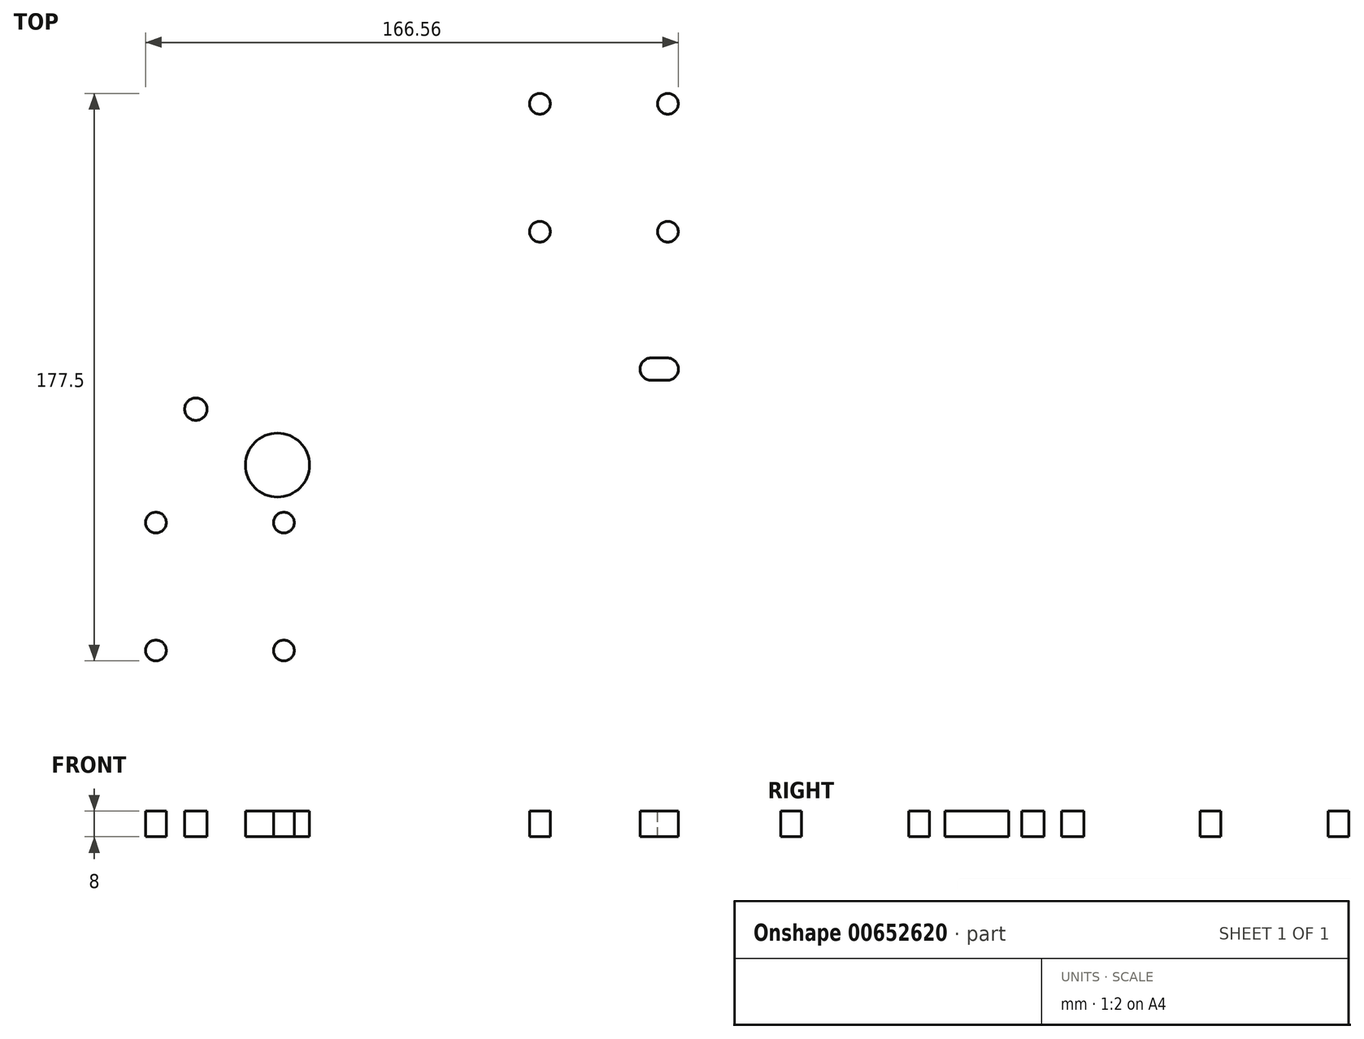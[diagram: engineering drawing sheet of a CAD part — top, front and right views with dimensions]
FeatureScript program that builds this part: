
annotation { "Feature Type Name" : "Feature", "Feature Type Description" : "" }
export const myFeature = defineFeature(function(context is Context, id is Id, definition is map)
    precondition{}
    {
        {
            var Q0;
            Q0=qCreatedBy(makeId("Top.planeOp"),FACE);
            var sketch = newSketch(context, id + "F0", { "sketchPlane" : qUnion([Q0])});
            skLineSegment(sketch, "E0.bottom", {"start": v(-87.5, 92.5) * mm, "end": v(87.5, 92.5) * mm});
            skLineSegment(sketch, "E0.top", {"start": v(-87.5, -92.5) * mm, "end": v(87.5, -92.5) * mm});
            skLineSegment(sketch, "E0.left", {"start": v(-87.5, 92.5) * mm, "end": v(-87.5, -92.5) * mm});
            skLineSegment(sketch, "E0.right", {"start": v(87.5, 92.5) * mm, "end": v(87.5, -92.5) * mm});
            skSolve(sketch);
        }
        {
            var Q0;
            Q0=makeQuery(id+"F0.imprint","IMPRINT",FACE,{"disambiguationData":[TD([[makeQuery(id+"F0.imprint","IMPRINT",EDGE,{"derivedFrom":sQuery(id+"F0.wireOp",EDGE,"E0.bottom")}),-1.0]])]});
            extrude(context, id + "F1", {"entities" : qUnion([Q0]), "oppositeDirection" : true, "depth" : 8 * mm, "offsetDistance" : 25 * mm});
        }
        {
            var Q0;
            Q0=makeQuery(id+"F1.opExtrude","CAP_FACE",FACE,{"disambiguationData":[OSD([sQuery(id+"F0.wireOp",EDGE,"E0.bottom"),sQuery(id+"F0.wireOp",EDGE,"E0.top"),sQuery(id+"F0.wireOp",EDGE,"E0.left"),sQuery(id+"F0.wireOp",EDGE,"E0.right")])],"isStart":true});
            var sketch = newSketch(context, id + "F2", { "sketchPlane" : qUnion([Q0])});
            skCircle(sketch, "E1", {"center": v(40, -85.5) * mm, "radius": 3.25 * mm});
            skCircle(sketch, "E2", {"center": v(80, -85.5) * mm, "radius": 3.25 * mm});
            skCircle(sketch, "E3", {"center": v(42, -27.5) * mm, "radius": 10 * mm});
            skCircle(sketch, "E4", {"center": v(40, -45.5) * mm, "radius": 3.25 * mm});
            skCircle(sketch, "E5", {"center": v(80, -45.5) * mm, "radius": 3.25 * mm});
            skCircle(sketch, "E6", {"center": v(0, -42.5) * mm, "radius": 20 * mm});
            skCircle(sketch, "E7.MirrorC", {"center": v(40, 85.5) * mm, "radius": 3.25 * mm});
            skCircle(sketch, "E8.MirrorC", {"center": v(80, 85.5) * mm, "radius": 3.25 * mm});
            skCircle(sketch, "E9.MirrorC", {"center": v(40, 45.5) * mm, "radius": 3.25 * mm});
            skCircle(sketch, "E10.MirrorC", {"center": v(80, 45.5) * mm, "radius": 3.25 * mm});
            skCircle(sketch, "E11.MirrorC", {"center": v(-80, 85.5) * mm, "radius": 3.25 * mm});
            skCircle(sketch, "E12.MirrorC", {"center": v(-80, 45.5) * mm, "radius": 3.25 * mm});
            skCircle(sketch, "E13.MirrorC", {"center": v(-40, 45.5) * mm, "radius": 3.25 * mm});
            skCircle(sketch, "E14.MirrorC", {"center": v(-40, 85.5) * mm, "radius": 3.25 * mm});
            skCircle(sketch, "E15.MirrorC", {"center": v(-40, -85.5) * mm, "radius": 3.25 * mm});
            skCircle(sketch, "E16.MirrorC", {"center": v(-40, -45.5) * mm, "radius": 3.25 * mm});
            skCircle(sketch, "E17.MirrorC", {"center": v(-80, -45.5) * mm, "radius": 3.25 * mm});
            skCircle(sketch, "E18.MirrorC", {"center": v(-80, -85.5) * mm, "radius": 3.25 * mm});
            skCircle(sketch, "E19.MirrorC", {"center": v(-42, -27.5) * mm, "radius": 10 * mm});
            skCircle(sketch, "E20.MirrorC", {"center": v(-67.5, -10) * mm, "radius": 3.5 * mm});
            skArc(sketch, "E21", {"start": v(79.81, 29) * mm, "mid": v(83.31, 32.5) * mm, "end": v(79.81, 36) * mm});
            skLineSegment(sketch, "E22", {"start": v(74.81, 29) * mm, "end": v(79.81, 29) * mm});
            skLineSegment(sketch, "E23", {"start": v(77.31, 29) * mm, "end": v(77.31, 24.51) * mm});
            skLineSegment(sketch, "E24.MirrorCS", {"start": v(74.81, 36) * mm, "end": v(79.81, 36) * mm});
            skArc(sketch, "E25", {"start": v(74.81, 36) * mm, "mid": v(71.31, 32.5) * mm, "end": v(74.81, 29) * mm});
            skArc(sketch, "E26.MirrorCS", {"start": v(79.81, 6) * mm, "mid": v(83.31, 2.5) * mm, "end": v(79.81, -1) * mm});
            skLineSegment(sketch, "E27.MirrorCS", {"start": v(74.81, -1) * mm, "end": v(79.81, -1) * mm});
            skLineSegment(sketch, "E28.MirrorCS", {"start": v(74.81, 6) * mm, "end": v(79.81, 6) * mm});
            skArc(sketch, "E29.MirrorCS", {"start": v(74.81, -1) * mm, "mid": v(71.31, 2.5) * mm, "end": v(74.81, 6) * mm});
            skCircle(sketch, "E30", {"center": v(67.5, -75) * mm, "radius": 3 * mm});
            skCircle(sketch, "E31.MirrorC", {"center": v(-67.5, -75) * mm, "radius": 3 * mm});
            skLineSegment(sketch, "E32", {"start": v(0, 0) * mm, "end": v(0, -134.36) * mm, "construction": true});
            skCircle(sketch, "E33", {"center": v(67.5, -10) * mm, "radius": 3.5 * mm});
            skSolve(sketch);
        }
        {
            var Q0;
            Q0=makeQuery(id+"F2.imprint","IMPRINT",FACE,{"disambiguationData":[TD([[makeQuery(id+"F2.imprint","IMPRINT",EDGE,{"derivedFrom":sQuery(id+"F2.wireOp",EDGE,"E11.MirrorC")}),1.0]])]});
            var Q1;
            Q1=makeQuery(id+"F2.imprint","IMPRINT",FACE,{"disambiguationData":[TD([[makeQuery(id+"F2.imprint","IMPRINT",EDGE,{"derivedFrom":sQuery(id+"F2.wireOp",EDGE,"E14.MirrorC")}),1.0]])]});
            var Q2;
            Q2=makeQuery(id+"F2.imprint","IMPRINT",FACE,{"disambiguationData":[TD([[makeQuery(id+"F2.imprint","IMPRINT",EDGE,{"derivedFrom":sQuery(id+"F2.wireOp",EDGE,"E13.MirrorC")}),1.0]])]});
            var Q3;
            Q3=makeQuery(id+"F2.imprint","IMPRINT",FACE,{"disambiguationData":[TD([[makeQuery(id+"F2.imprint","IMPRINT",EDGE,{"derivedFrom":sQuery(id+"F2.wireOp",EDGE,"E12.MirrorC")}),1.0]])]});
            var Q4;
            Q4=makeQuery(id+"F2.imprint","IMPRINT",FACE,{"disambiguationData":[TD([[makeQuery(id+"F2.imprint","IMPRINT",EDGE,{"derivedFrom":sQuery(id+"F2.wireOp",EDGE,"E7.MirrorC")}),-1.0]])]});
            var Q5;
            Q5=makeQuery(id+"F2.imprint","IMPRINT",FACE,{"disambiguationData":[TD([[makeQuery(id+"F2.imprint","IMPRINT",EDGE,{"derivedFrom":sQuery(id+"F2.wireOp",EDGE,"E8.MirrorC")}),-1.0]])]});
            var Q6;
            Q6=makeQuery(id+"F2.imprint","IMPRINT",FACE,{"disambiguationData":[TD([[makeQuery(id+"F2.imprint","IMPRINT",EDGE,{"derivedFrom":sQuery(id+"F2.wireOp",EDGE,"E9.MirrorC")}),-1.0]])]});
            var Q7;
            Q7=makeQuery(id+"F2.imprint","IMPRINT",FACE,{"disambiguationData":[TD([[makeQuery(id+"F2.imprint","IMPRINT",EDGE,{"derivedFrom":sQuery(id+"F2.wireOp",EDGE,"E10.MirrorC")}),-1.0]])]});
            var Q8;
            {var subQ1=sQuery(id+"F2.wireOp",EDGE,"E21");Q8=makeQuery(id+"F2.imprint","IMPRINT",FACE,{"disambiguationData":[TD([[makeQuery(id+"F2.imprint","IMPRINT",EDGE,{"derivedFrom":subQ1}),1.0]])]});}
            var Q9;
            Q9=makeQuery(id+"F2.imprint","IMPRINT",FACE,{"disambiguationData":[TD([[makeQuery(id+"F2.imprint","IMPRINT",EDGE,{"derivedFrom":sQuery(id+"F2.wireOp",EDGE,"E26.MirrorCS")}),-1.0]])]});
            var Q10;
            Q10=makeQuery(id+"F2.imprint","IMPRINT",FACE,{"disambiguationData":[TD([[makeQuery(id+"F2.imprint","IMPRINT",EDGE,{"derivedFrom":sQuery(id+"F2.wireOp",EDGE,"fSzb9bLY-MCyR-M5rw-Yt1T-PzNvFZUMUZM1")}),1.0]])]});
            var Q11;
            Q11=makeQuery(id+"F2.imprint","IMPRINT",FACE,{"disambiguationData":[TD([[makeQuery(id+"F2.imprint","IMPRINT",EDGE,{"derivedFrom":sQuery(id+"F2.wireOp",EDGE,"E3")}),1.0]])]});
            var Q12;
            Q12=makeQuery(id+"F2.imprint","IMPRINT",FACE,{"disambiguationData":[TD([[makeQuery(id+"F2.imprint","IMPRINT",EDGE,{"derivedFrom":sQuery(id+"F2.wireOp",EDGE,"E4")}),1.0]])]});
            var Q13;
            Q13=makeQuery(id+"F2.imprint","IMPRINT",FACE,{"disambiguationData":[TD([[makeQuery(id+"F2.imprint","IMPRINT",EDGE,{"derivedFrom":sQuery(id+"F2.wireOp",EDGE,"E2")}),1.0]])]});
            var Q14;
            Q14=makeQuery(id+"F2.imprint","IMPRINT",FACE,{"disambiguationData":[TD([[makeQuery(id+"F2.imprint","IMPRINT",EDGE,{"derivedFrom":sQuery(id+"F2.wireOp",EDGE,"E5")}),1.0]])]});
            var Q15;
            Q15=makeQuery(id+"F2.imprint","IMPRINT",FACE,{"disambiguationData":[TD([[makeQuery(id+"F2.imprint","IMPRINT",EDGE,{"derivedFrom":sQuery(id+"F2.wireOp",EDGE,"E1")}),1.0]])]});
            var Q16;
            Q16=makeQuery(id+"F2.imprint","IMPRINT",FACE,{"disambiguationData":[TD([[makeQuery(id+"F2.imprint","IMPRINT",EDGE,{"derivedFrom":sQuery(id+"F2.wireOp",EDGE,"E15.MirrorC")}),-1.0]])]});
            var Q17;
            Q17=makeQuery(id+"F2.imprint","IMPRINT",FACE,{"disambiguationData":[TD([[makeQuery(id+"F2.imprint","IMPRINT",EDGE,{"derivedFrom":sQuery(id+"F2.wireOp",EDGE,"E18.MirrorC")}),-1.0]])]});
            var Q18;
            Q18=makeQuery(id+"F2.imprint","IMPRINT",FACE,{"disambiguationData":[TD([[makeQuery(id+"F2.imprint","IMPRINT",EDGE,{"derivedFrom":sQuery(id+"F2.wireOp",EDGE,"E17.MirrorC")}),-1.0]])]});
            var Q19;
            Q19=makeQuery(id+"F2.imprint","IMPRINT",FACE,{"disambiguationData":[TD([[makeQuery(id+"F2.imprint","IMPRINT",EDGE,{"derivedFrom":sQuery(id+"F2.wireOp",EDGE,"E16.MirrorC")}),-1.0]])]});
            var Q20;
            Q20=makeQuery(id+"F2.imprint","IMPRINT",FACE,{"disambiguationData":[TD([[makeQuery(id+"F2.imprint","IMPRINT",EDGE,{"derivedFrom":sQuery(id+"F2.wireOp",EDGE,"E19.MirrorC")}),-1.0]])]});
            var Q21;
            Q21=makeQuery(id+"F2.imprint","IMPRINT",FACE,{"disambiguationData":[TD([[makeQuery(id+"F2.imprint","IMPRINT",EDGE,{"derivedFrom":sQuery(id+"F2.wireOp",EDGE,"E20.MirrorC")}),-1.0]])]});
            var Q22;
            Q22=makeQuery(id+"F2.imprint","IMPRINT",FACE,{"disambiguationData":[TD([[makeQuery(id+"F2.imprint","IMPRINT",EDGE,{"derivedFrom":sQuery(id+"F2.wireOp",EDGE,"E6")}),1.0]])]});
            var Q23;
            Q23=makeQuery(id+"F2.imprint","IMPRINT",FACE,{"disambiguationData":[TD([[makeQuery(id+"F2.imprint","IMPRINT",EDGE,{"derivedFrom":sQuery(id+"F2.wireOp",EDGE,"E33")}),1.0]])]});
            extrude(context, id + "F3", {"entities" : qUnion([Q0, Q1, Q2, Q3, Q4, Q5, Q6, Q7, Q8, Q9, Q10, Q11, Q12, Q13, Q14, Q15, Q16, Q17, Q18, Q19, Q20, Q21, Q22, Q23]), "operationType" : NewBodyOperationType.REMOVE, "oppositeDirection" : true, "depth" : 25 * mm, "offsetDistance" : 25 * mm});
        }
        {
            var Q0;
            Q0=makeQuery(id+"F1.opExtrude","CAP_FACE",FACE,{"disambiguationData":[OSD([sQuery(id+"F0.wireOp",EDGE,"E0.bottom"),sQuery(id+"F0.wireOp",EDGE,"E0.top"),sQuery(id+"F0.wireOp",EDGE,"E0.left"),sQuery(id+"F0.wireOp",EDGE,"E0.right")])],"isStart":false});
            var sketch = newSketch(context, id + "F4", { "sketchPlane" : qUnion([Q0])});
            skCircle(sketch, "E34", {"center": v(-67.5, 75) * mm, "radius": 3 * mm});
            skCircle(sketch, "E35.MirrorC", {"center": v(67.5, 75) * mm, "radius": 3 * mm});
            skSolve(sketch);
        }
        {
            var Q0;
            Q0=sQuery(id+"F4.wireOp",VERTEX,"E34.center");
            var Q1;
            Q1=sQuery(id+"F4.wireOp",VERTEX,"E35.MirrorC.center");
            var Q2;
            Q2=makeQuery(id+"F1.opExtrude","SWEPT_BODY",BODY,{"disambiguationData":[OSD([sQuery(id+"F0.wireOp",EDGE,"E0.bottom"),sQuery(id+"F0.wireOp",EDGE,"E0.top"),sQuery(id+"F0.wireOp",EDGE,"E0.left"),sQuery(id+"F0.wireOp",EDGE,"E0.right")])]});
            hole(context, id + "F5", {"style" : HoleStyle.C_BORE, "endStyle" : HoleEndStyle.BLIND, "holeDiameter" : 6 * mm, "cBoreDiameter" : 10 * mm, "cBoreDepth" : 5 * mm, "majorDiameter" : 5 * mm, "holeDepth" : 15 * mm, "isTappedThrough" : true, "tappedDepth" : 12 * mm, "tapClearance" : 3, "locations" : qUnion([Q0, Q1]), "scope" : qUnion([Q2])});
        }
    });
